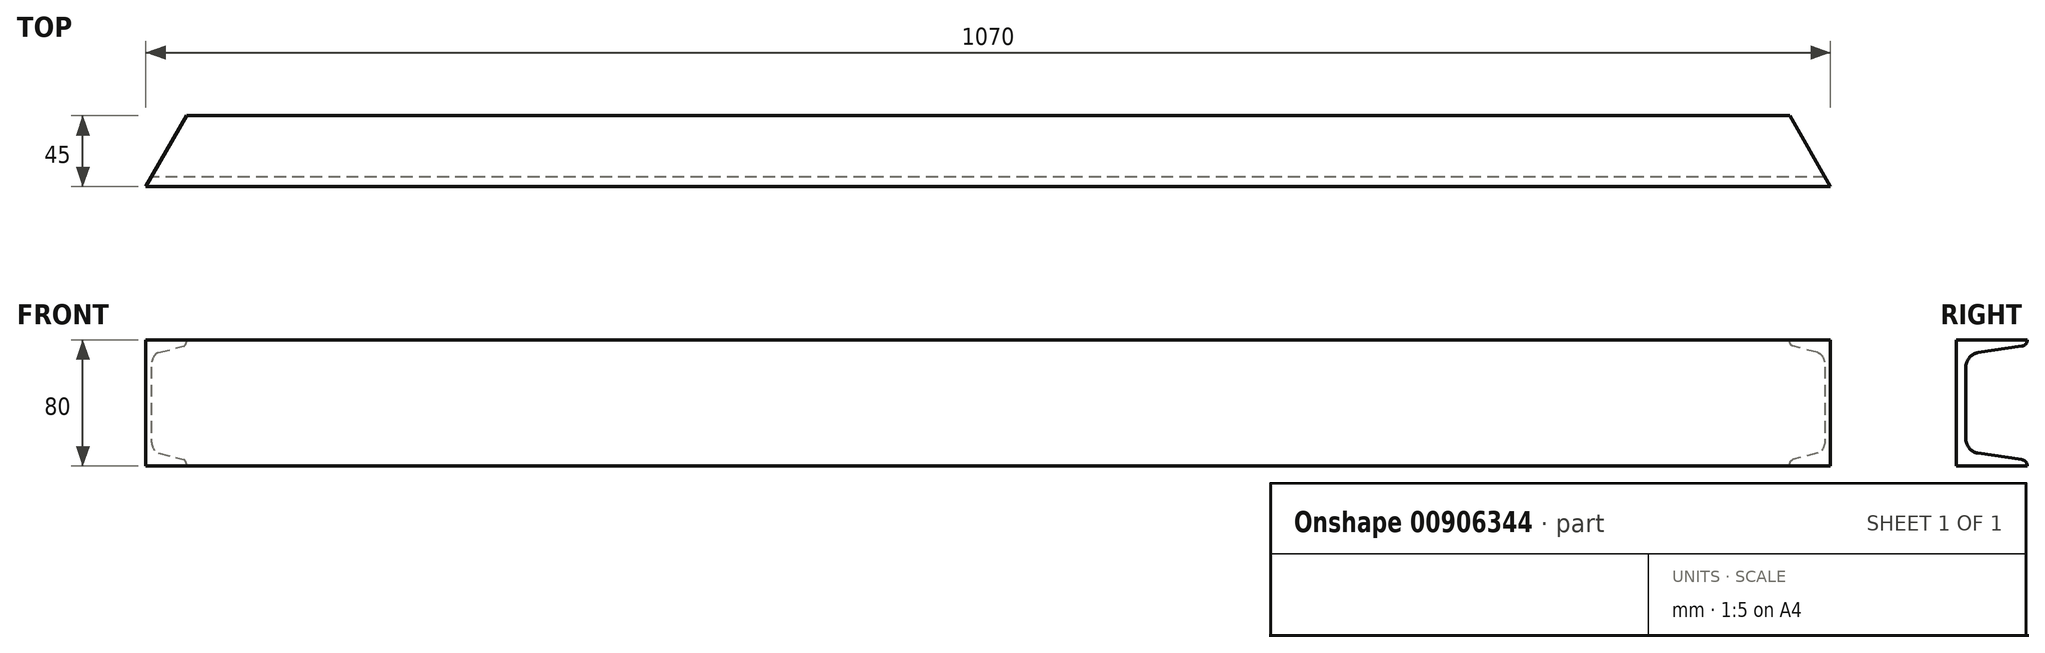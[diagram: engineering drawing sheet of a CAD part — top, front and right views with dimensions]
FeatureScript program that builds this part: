
annotation { "Feature Type Name" : "Feature", "Feature Type Description" : "" }
export const myFeature = defineFeature(function(context is Context, id is Id, definition is map)
    precondition{}
    {
        {
            var Q0;
            Q0=qCreatedBy(makeId("Top.planeOp"),FACE);
            var sketch = newSketch(context, id + "F0", { "sketchPlane" : qUnion([Q0])});
            skLineSegment(sketch, "E0", {"start": v(-794.5, 0) * mm, "end": v(794.5, 0) * mm});
            skLineSegment(sketch, "E1", {"start": v(794.5, 0) * mm, "end": v(768.52, 45) * mm});
            skLineSegment(sketch, "E2", {"start": v(768.52, 45) * mm, "end": v(-768.52, 45) * mm});
            skLineSegment(sketch, "E3", {"start": v(-768.52, 45) * mm, "end": v(-794.5, 0) * mm});
            skLineSegment(sketch, "E4", {"start": v(0, 220.63) * mm, "end": v(0, 0) * mm, "construction": true});
            skSolve(sketch);
        }
        {
            var Q0;
            Q0=qCreatedBy(makeId("Right.planeOp"),FACE);
            var sketch = newSketch(context, id + "F1", { "sketchPlane" : qUnion([Q0])});
            skLineSegment(sketch, "E5", {"start": v(0, 40) * mm, "end": v(0, 80) * mm});
            skLineSegment(sketch, "E6", {"start": v(0, 80) * mm, "end": v(45, 80) * mm});
            skPoint(sketch, "E7.startSnap0", {"position": v(0, 40) * mm});
            skLineSegment(sketch, "E8", {"start": v(0, 40) * mm, "end": v(15, 40) * mm});
            skLineSegment(sketch, "E9", {"start": v(15, 40) * mm, "end": v(15, 63) * mm, "construction": true});
            skLineSegment(sketch, "E10", {"start": v(15, 40) * mm, "end": v(15, 17) * mm, "construction": true});
            skLineSegment(sketch, "E11", {"start": v(6, 63) * mm, "end": v(6, 40) * mm});
            skArc(sketch, "E12", {"start": v(13.68, 71.9) * mm, "mid": v(8.19, 68.88) * mm, "end": v(6, 63) * mm});
            skArc(sketch, "E13", {"start": v(41.59, 76.04) * mm, "mid": v(44.03, 77.39) * mm, "end": v(45, 80) * mm});
            skLineSegment(sketch, "E14", {"start": v(13.68, 71.9) * mm, "end": v(41.59, 76.04) * mm});
            skArc(sketch, "E15.MirrorCS", {"start": v(13.68, 8.1) * mm, "mid": v(8.19, 11.12) * mm, "end": v(6, 17) * mm});
            skLineSegment(sketch, "E16.MirrorCS", {"start": v(0, 40) * mm, "end": v(0, 0) * mm});
            skLineSegment(sketch, "E17.MirrorCS", {"start": v(0, 0) * mm, "end": v(45, 0) * mm});
            skLineSegment(sketch, "E18.MirrorCS", {"start": v(6, 17) * mm, "end": v(6, 40) * mm});
            skArc(sketch, "E19.MirrorCS", {"start": v(41.59, 3.96) * mm, "mid": v(44.03, 2.61) * mm, "end": v(45, 0) * mm});
            skLineSegment(sketch, "E20.MirrorCS", {"start": v(13.68, 8.1) * mm, "end": v(41.59, 3.96) * mm});
            skSolve(sketch);
        }
        {
            var Q0;
            Q0=qSketchRegion(id+"F1",true);
            extrude(context, id + "F2", {"entities" : qUnion([Q0]), "endBound" : BoundingType.SYMMETRIC, "depth" : 1070 * mm, "offsetDistance" : 25 * mm});
        }
        {
            var Q0;
            Q0=makeQuery(id+"F2.opExtrude","SWEPT_FACE",FACE,{"disambiguationData":[OSD([sQuery(id+"F1.wireOp",EDGE,"E6")])]});
            var sketch = newSketch(context, id + "F3", { "sketchPlane" : qUnion([Q0])});
            skLineSegment(sketch, "E21", {"start": v(-535, 0) * mm, "end": v(-509.02, 45) * mm});
            skLineSegment(sketch, "E22", {"start": v(-509.02, 45) * mm, "end": v(-535, 45) * mm});
            skLineSegment(sketch, "E23", {"start": v(-535, 45) * mm, "end": v(-535, 0) * mm});
            skLineSegment(sketch, "E24.MirrorCS", {"start": v(509.02, 45) * mm, "end": v(535, 45) * mm});
            skLineSegment(sketch, "E25.MirrorCS", {"start": v(535, 45) * mm, "end": v(535, 0) * mm});
            skLineSegment(sketch, "E26.MirrorCS", {"start": v(535, 0) * mm, "end": v(509.02, 45) * mm});
            skSolve(sketch);
        }
        {
            var Q0;
            Q0=qSketchRegion(id+"F3",true);
            var Q1;
            Q1=makeQuery(id+"F2.opExtrude","SWEPT_FACE",FACE,{"disambiguationData":[OSD([sQuery(id+"F1.wireOp",EDGE,"E17.MirrorCS")])]});
            extrude(context, id + "F4", {"entities" : qUnion([Q0]), "operationType" : NewBodyOperationType.REMOVE, "endBound" : BoundingType.UP_TO_SURFACE, "oppositeDirection" : true, "depth" : 25 * mm, "endBoundEntityFace" : qUnion([Q1]), "offsetDistance" : 25 * mm});
        }
    });
